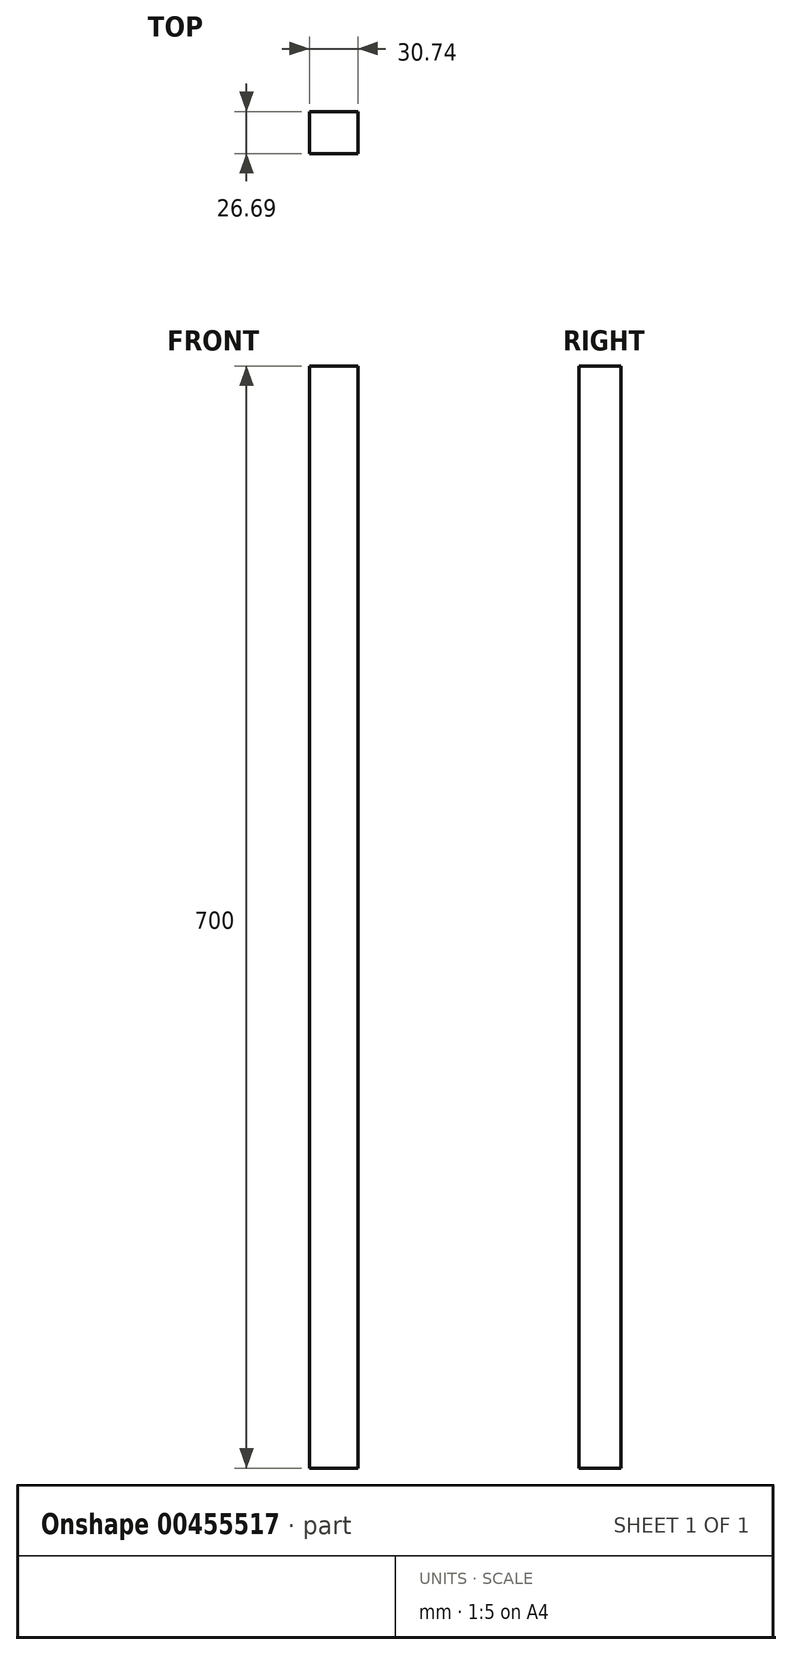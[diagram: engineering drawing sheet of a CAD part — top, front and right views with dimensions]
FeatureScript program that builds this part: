
annotation { "Feature Type Name" : "Feature", "Feature Type Description" : "" }
export const myFeature = defineFeature(function(context is Context, id is Id, definition is map)
    precondition{}
    {
        {
            var Q0;
            Q0=qCreatedBy(makeId("Top.planeOp"),FACE);
            var sketch = newSketch(context, id + "F0", { "sketchPlane" : qUnion([Q0])});
            skLineSegment(sketch, "E0.bottom", {"start": v(0, 20.93) * mm, "end": v(30.74, 20.93) * mm});
            skLineSegment(sketch, "E0.top", {"start": v(0, -5.76) * mm, "end": v(30.74, -5.76) * mm});
            skLineSegment(sketch, "E0.left", {"start": v(0, 20.93) * mm, "end": v(0, -5.76) * mm});
            skLineSegment(sketch, "E0.right", {"start": v(30.74, 20.93) * mm, "end": v(30.74, -5.76) * mm});
            skSolve(sketch);
        }
        {
            var Q0;
            Q0=makeQuery(id+"F0.imprint","IMPRINT",FACE,{"disambiguationData":[TD([[makeQuery(id+"F0.imprint","IMPRINT",EDGE,{"derivedFrom":sQuery(id+"F0.wireOp",EDGE,"E0.bottom")}),-1.0]])]});
            extrude(context, id + "F1", {"entities" : qUnion([Q0]), "depth" : 700 * mm, "hasSecondDirectionDraft" : true, "secondDirectionDraftAngle" : 3 * degree, "secondDirectionDraftPullDirection" : true});
        }
    });
